# Revit family: NLRS_33_RB_DO_BILCO_dakluik_F-50TB
name_source: partatom
category: Doors
revit_build: Autodesk Revit 2015 (Build: 20140223_1515(x64)
units: mm (PartAtom-declared; Revit-internal decimal feet)

## types (1)
- NLRS_33_RB_DO_BILCO_dakluik_F-50TB
    Description = standaard aluminium dakluik
    Height = 405 mm  [stored 1.32874 ft]
    Length = 1500 mm  [stored 4.92126 ft]
    Manufacturer = Bilco
    Model = F-50TB
    RWA = No
    Rough Height = 0 mm  [stored 0 ft]
    Rough Width = 0 mm  [stored 0 ft]
    Thickness = 0 mm  [stored 0 ft]
    Width = 1500 mm  [stored 4.92126 ft]
    bediening = handmatig
    belasting = 195.00 kg/m²
    brandwerend 120 min = No
    brandwerend 30 min = No
    brandwerend 60 min = No
    brandwerend 90 min = No
    breedte = 1500 mm  [stored 4.92126 ft]
    breedte paneel = 1410 mm
    cilinderslot = No
    code productgroep = LUI
    conservering = brut
    dagmaatbreedte = 1220 mm  [stored 4.00262 ft]
    dagmaatlengte = 1220 mm  [stored 4.00262 ft]
    deurblad = vlak
    dikte_isolatie = 75 mm
    false = No
    geluidsreductie (dB) = 25
    gewicht (kg) = 126
    hoogte = 405 mm  [stored 1.32874 ft]
    hoogte opstand = 305 mm  [stored 1.00066 ft]
    hoogte_aandrijving = 323 mm  [stored 1.05971 ft]
    isolatie = Yes
    isolatiedikte = 75 mm
    isolatiewaarde = 3.5900 (m²·K)/W
    lengte = 1500 mm  [stored 4.92126 ft]
    lengte paneel = 1410 mm
    loopslot = Yes
    materiaal = bcb_aluminium
    netto doorlaat = 0 m²
    omranding blokkozijn = No
    omranding dakopstand = Yes
    omranding hoekprofiel = No
    omranding waterafvoerend = No
    omschrijving = standaard aluminium dakluik
    openingshoek = 90.00°
    openstand vergrendeling = Yes
    plaatdikte = 2 mm  [stored 0.00656168 ft]
    productgroep = Dakluiken
    scharnierend = Yes
    thermische onderbreking = Yes
    true = Yes
    veersysteem = Yes
    veiligheidsrailing = Yes
    waterdicht = Yes

note: [stored X ft] marks values corroborated as IEEE doubles in the binary element streams (Revit-internal decimal feet)

## geometry (parser evidence)
native form markers: Sweep x16
no freeform markers — native parametric forms only
